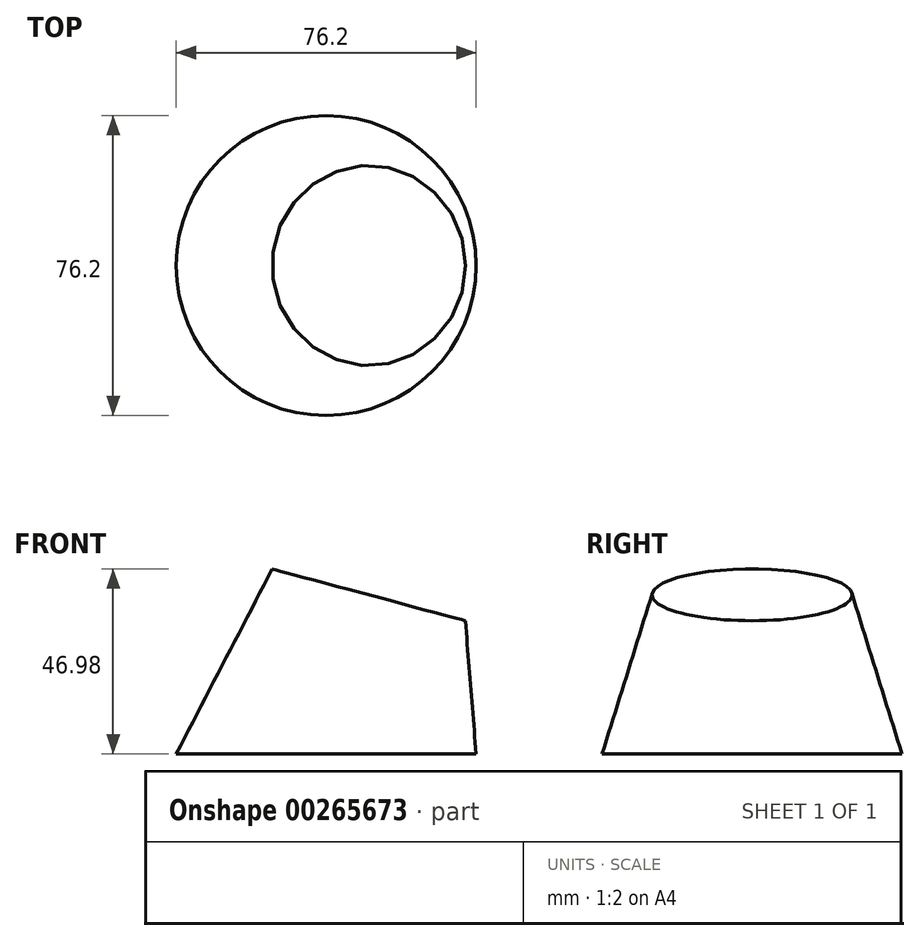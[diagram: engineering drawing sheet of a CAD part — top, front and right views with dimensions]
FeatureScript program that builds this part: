
annotation { "Feature Type Name" : "Feature", "Feature Type Description" : "" }
export const myFeature = defineFeature(function(context is Context, id is Id, definition is map)
    precondition{}
    {
        {
            var Q0;
            Q0=qCreatedBy(makeId("Top.planeOp"),FACE);
            var sketch = newSketch(context, id + "F0", { "sketchPlane" : qUnion([Q0])});
            skLineSegment(sketch, "E0.bottom", {"start": v(-63.5, 63.5) * mm, "end": v(63.5, 63.5) * mm});
            skLineSegment(sketch, "E0.top", {"start": v(-63.5, -63.5) * mm, "end": v(63.5, -63.5) * mm});
            skLineSegment(sketch, "E0.left", {"start": v(-63.5, 63.5) * mm, "end": v(-63.5, -63.5) * mm});
            skLineSegment(sketch, "E0.right", {"start": v(63.5, 63.5) * mm, "end": v(63.5, -63.5) * mm});
            skPoint(sketch, "E0.middle", {"position": v(0, 0) * mm});
            skCircle(sketch, "E1", {"center": v(0, 0) * mm, "radius": 38.1 * mm});
            skSolve(sketch);
        }
        {
            var Q0;
            Q0=qCreatedBy(makeId("Top.planeOp"),FACE);
            var Q1;
            Q1=sQuery(id+"F0.wireOp",EDGE,"E0.right");
            cPlane(context, id + "F1", {"entities" : qUnion([Q0, Q1]), "cplaneType" : CPlaneType.LINE_ANGLE, "offset" : 25.4 * mm, "angle" : 15 * degree, "oppositeDirection" : true, "width" : 152.4 * mm, "height" : 152.4 * mm});
        }
        {
            var Q0;
            Q0=qCreatedBy(id+"F1.planeOp",FACE);
            cPlane(context, id + "F2", {"entities" : qUnion([Q0]), "cplaneType" : CPlaneType.OFFSET, "offset" : 25.4 * mm, "oppositeDirection" : true, "width" : 152.4 * mm, "height" : 152.4 * mm});
        }
        {
            var Q0;
            Q0=qCreatedBy(id+"F2.planeOp",FACE);
            var sketch = newSketch(context, id + "F3", { "sketchPlane" : qUnion([Q0])});
            skCircle(sketch, "E2", {"center": v(0, 0) * mm, "radius": 25.4 * mm});
            skSolve(sketch);
        }
        {
            var Q0;
            Q0=makeQuery(id+"F0.imprint","IMPRINT",FACE,{"disambiguationData":[TD([[makeQuery(id+"F0.imprint","IMPRINT",EDGE,{"derivedFrom":sQuery(id+"F0.wireOp",EDGE,"E1")}),1.0]])]});
            var Q1;
            Q1=makeQuery(id+"F3.imprint","IMPRINT",FACE,{"disambiguationData":[TD([[makeQuery(id+"F3.imprint","IMPRINT",EDGE,{"derivedFrom":sQuery(id+"F3.wireOp",EDGE,"E2")}),1.0]])]});
            loft(context, id + "F4", {"sheetProfilesArray" : [{ "sheetProfileEntities" : qUnion([Q0]) }, { "sheetProfileEntities" : qUnion([Q1]) }]});
        }
    });
